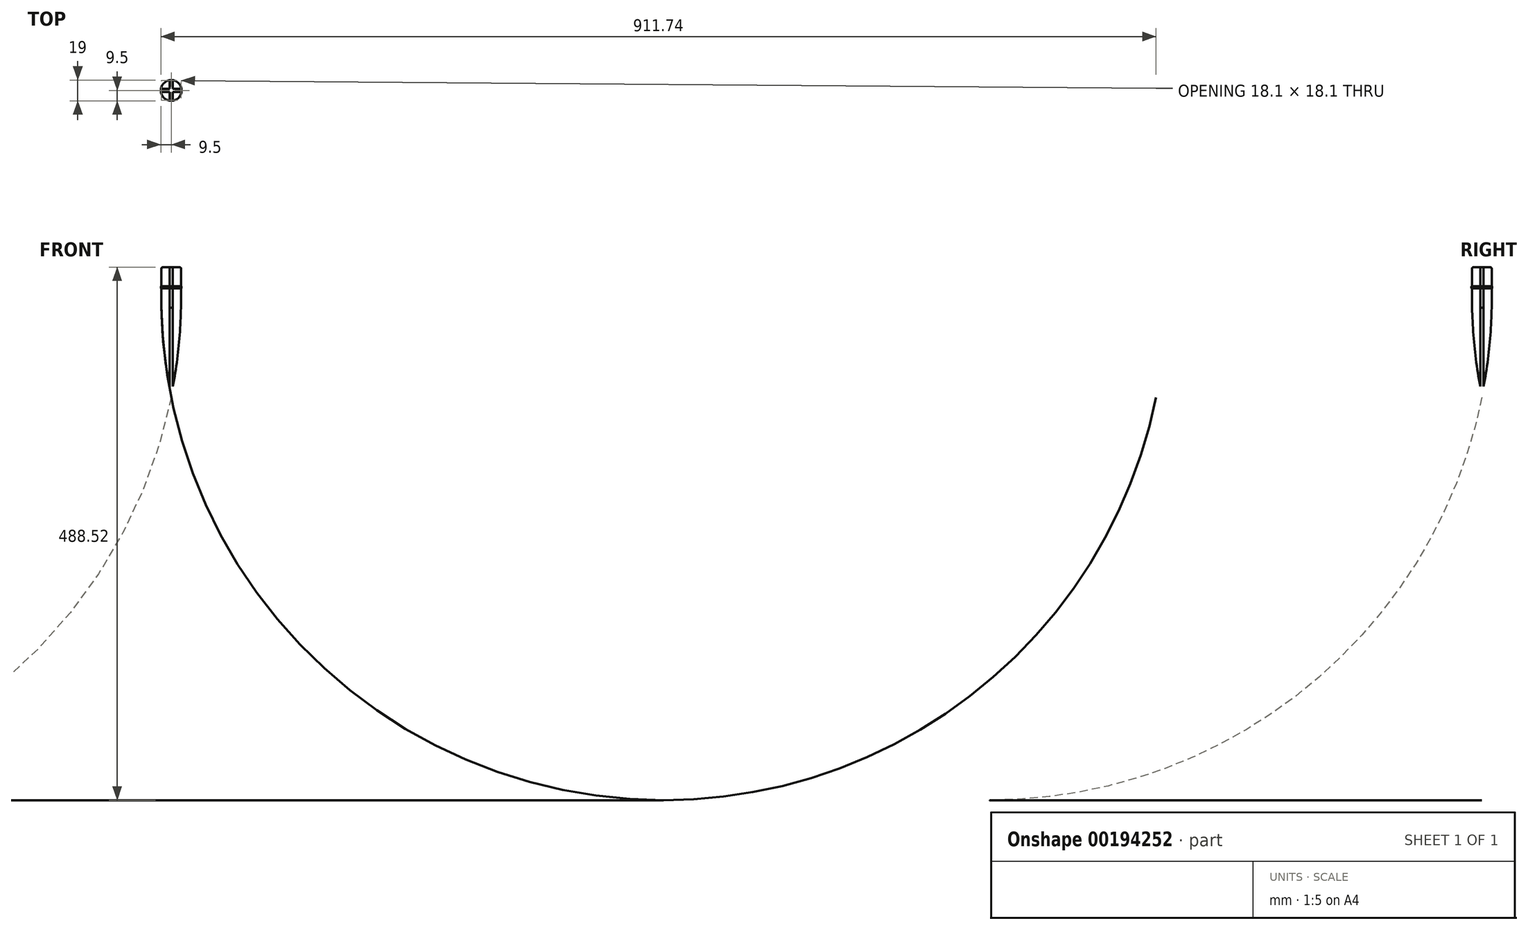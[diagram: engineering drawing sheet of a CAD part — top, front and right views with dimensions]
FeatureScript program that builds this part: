
annotation { "Feature Type Name" : "Feature", "Feature Type Description" : "" }
export const myFeature = defineFeature(function(context is Context, id is Id, definition is map)
    precondition{}
    {
        {
            var Q0;
            Q0=qCreatedBy(makeId("Top.planeOp"),FACE);
            var sketch = newSketch(context, id + "F0", { "sketchPlane" : qUnion([Q0])});
            skCircle(sketch, "E0", {"center": v(0, 0) * mm, "radius": 9.05 * mm});
            skSolve(sketch);
        }
        {
            var Q0;
            Q0 = qSketchRegion(id + "F0", true);
            extrude(context, id + "F1", {"entities" : qUnion([Q0]), "depth" : 17.5 * mm});
        }
        {
            var Q0;
            Q0=makeQuery(id+"F1.opExtrude","CAP_EDGE",EDGE,{"disambiguationData":[OSD([sQuery(id+"F0.wireOp",EDGE,"E0")])],"isStart":false});
            fillet(context, id + "F2", {"entities" : qUnion([Q0]), "radius" : 1.5 * mm, "tangentPropagation" : true, "allowEdgeOverflow" : false});
        }
        {
            var Q0;
            Q0=makeQuery(id+"F1.opExtrude","CAP_FACE",FACE,{"disambiguationData":[OSD([sQuery(id+"F0.wireOp",EDGE,"E0")])],"isStart":true});
            var sketch = newSketch(context, id + "F3", { "sketchPlane" : qUnion([Q0])});
            skLineSegment(sketch, "E1", {"start": v(9.05, 1.4) * mm, "end": v(0, 1.4) * mm});
            skLineSegment(sketch, "E2", {"start": v(9.05, 1.4) * mm, "end": v(9.05, 0) * mm});
            skLineSegment(sketch, "E3.MirrorCS", {"start": v(1.4, 9.05) * mm, "end": v(1.4, 0) * mm});
            skLineSegment(sketch, "E4.MirrorCS", {"start": v(1.4, 9.05) * mm, "end": v(0, 9.05) * mm});
            skLineSegment(sketch, "E5.MirrorCS", {"start": v(-9.05, 1.4) * mm, "end": v(0, 1.4) * mm});
            skLineSegment(sketch, "E6.MirrorCS", {"start": v(-1.4, 9.05) * mm, "end": v(-1.4, 0) * mm});
            skLineSegment(sketch, "E7.MirrorCS", {"start": v(-1.4, 9.05) * mm, "end": v(0, 9.05) * mm});
            skLineSegment(sketch, "E8.MirrorCS", {"start": v(-9.05, 1.4) * mm, "end": v(-9.05, 0) * mm});
            skLineSegment(sketch, "E9.MirrorCS", {"start": v(9.05, -1.4) * mm, "end": v(0, -1.4) * mm});
            skLineSegment(sketch, "E10.MirrorCS", {"start": v(-9.05, -1.4) * mm, "end": v(0, -1.4) * mm});
            skLineSegment(sketch, "E11.MirrorCS", {"start": v(1.4, -9.05) * mm, "end": v(1.4, 0) * mm});
            skLineSegment(sketch, "E12.MirrorCS", {"start": v(-1.4, -9.05) * mm, "end": v(-1.4, 0) * mm});
            skLineSegment(sketch, "E13.MirrorCS", {"start": v(1.4, -9.05) * mm, "end": v(0, -9.05) * mm});
            skLineSegment(sketch, "E14.MirrorCS", {"start": v(-1.4, -9.05) * mm, "end": v(0, -9.05) * mm});
            skLineSegment(sketch, "E15.MirrorCS", {"start": v(9.05, -1.4) * mm, "end": v(9.05, 0) * mm});
            skLineSegment(sketch, "E16.MirrorCS", {"start": v(-9.05, -1.4) * mm, "end": v(-9.05, 0) * mm});
            skArc(sketch, "E17", {"start": v(9.05, 1.4) * mm, "mid": v(7.85, 7.85) * mm, "end": v(1.4, 9.05) * mm});
            skArc(sketch, "E18", {"start": v(1.4, -9.05) * mm, "mid": v(8.37, -8.37) * mm, "end": v(9.05, -1.4) * mm});
            skArc(sketch, "E19", {"start": v(-9.05, -1.4) * mm, "mid": v(-7.92, -7.92) * mm, "end": v(-1.4, -9.05) * mm});
            skArc(sketch, "E20", {"start": v(-1.4, 9.05) * mm, "mid": v(-11.13, 11.13) * mm, "end": v(-9.05, 1.4) * mm});
            skSolve(sketch);
        }
        {
            var Q0;
            {var subQ0=sQuery(id+"F3.wireOp",EDGE,"E2");Q0=makeQuery(id+"F3.imprint","IMPRINT",FACE,{"disambiguationData":[TD([[makeQuery(id+"F3.imprint","IMPRINT",EDGE,{"derivedFrom":subQ0}),-1.0]])]});}
            var Q1;
            {var subQ0=sQuery(id+"F3.wireOp",EDGE,"E4.MirrorCS");Q1=makeQuery(id+"F3.imprint","IMPRINT",FACE,{"disambiguationData":[TD([[makeQuery(id+"F3.imprint","IMPRINT",EDGE,{"derivedFrom":subQ0}),1.0]])]});}
            var Q2;
            {var subQ0=sQuery(id+"F3.wireOp",EDGE,"E8.MirrorCS");Q2=makeQuery(id+"F3.imprint","IMPRINT",FACE,{"disambiguationData":[TD([[makeQuery(id+"F3.imprint","IMPRINT",EDGE,{"derivedFrom":subQ0}),1.0]])]});}
            var Q3;
            {var subQ0=sQuery(id+"F3.wireOp",EDGE,"E7.MirrorCS");Q3=makeQuery(id+"F3.imprint","IMPRINT",FACE,{"disambiguationData":[TD([[makeQuery(id+"F3.imprint","IMPRINT",EDGE,{"derivedFrom":subQ0}),-1.0]])]});}
            var Q4;
            {var subQ0=sQuery(id+"F3.wireOp",EDGE,"E15.MirrorCS");Q4=makeQuery(id+"F3.imprint","IMPRINT",FACE,{"disambiguationData":[TD([[makeQuery(id+"F3.imprint","IMPRINT",EDGE,{"derivedFrom":subQ0}),1.0]])]});}
            var Q5;
            {var subQ0=sQuery(id+"F3.wireOp",EDGE,"E16.MirrorCS");Q5=makeQuery(id+"F3.imprint","IMPRINT",FACE,{"disambiguationData":[TD([[makeQuery(id+"F3.imprint","IMPRINT",EDGE,{"derivedFrom":subQ0}),-1.0]])]});}
            var Q6;
            {var subQ0=sQuery(id+"F3.wireOp",EDGE,"E13.MirrorCS");Q6=makeQuery(id+"F3.imprint","IMPRINT",FACE,{"disambiguationData":[TD([[makeQuery(id+"F3.imprint","IMPRINT",EDGE,{"derivedFrom":subQ0}),-1.0]])]});}
            var Q7;
            {var subQ0=sQuery(id+"F3.wireOp",EDGE,"E14.MirrorCS");Q7=makeQuery(id+"F3.imprint","IMPRINT",FACE,{"disambiguationData":[TD([[makeQuery(id+"F3.imprint","IMPRINT",EDGE,{"derivedFrom":subQ0}),1.0]])]});}
            var Q8;
            {var subQ0=sQuery(id+"F3.wireOp",EDGE,"E3.MirrorCS");var subQ1=sQuery(id+"F3.wireOp",EDGE,"E1");var subQ2=makeQuery(id+"F3.imprint","INTERSECT",VERTEX,{"derivedFrom":[subQ1,subQ0]});Q8=makeQuery(id+"F3.imprint","IMPRINT",FACE,{"disambiguationData":[TD([[makeQuery(id+"F3.imprint","IMPRINT",EDGE,{"disambiguationData":[TD([[subQ2,1.0]])],"derivedFrom":subQ1}),-1.0]])]});}
            var Q9;
            {var subQ0=sQuery(id+"F3.wireOp",EDGE,"E11.MirrorCS");var subQ1=sQuery(id+"F3.wireOp",EDGE,"E9.MirrorCS");var subQ2=makeQuery(id+"F3.imprint","INTERSECT",VERTEX,{"derivedFrom":[subQ1,subQ0]});Q9=makeQuery(id+"F3.imprint","IMPRINT",FACE,{"disambiguationData":[TD([[makeQuery(id+"F3.imprint","IMPRINT",EDGE,{"disambiguationData":[TD([[subQ2,1.0]])],"derivedFrom":subQ1}),1.0]])]});}
            var Q10;
            {var subQ0=sQuery(id+"F3.wireOp",EDGE,"E12.MirrorCS");var subQ1=sQuery(id+"F3.wireOp",EDGE,"E10.MirrorCS");var subQ2=makeQuery(id+"F3.imprint","INTERSECT",VERTEX,{"derivedFrom":[subQ1,subQ0]});Q10=makeQuery(id+"F3.imprint","IMPRINT",FACE,{"disambiguationData":[TD([[makeQuery(id+"F3.imprint","IMPRINT",EDGE,{"disambiguationData":[TD([[subQ2,1.0]])],"derivedFrom":subQ1}),-1.0]])]});}
            var Q11;
            {var subQ0=sQuery(id+"F3.wireOp",EDGE,"E6.MirrorCS");var subQ1=sQuery(id+"F3.wireOp",EDGE,"E5.MirrorCS");var subQ2=makeQuery(id+"F3.imprint","INTERSECT",VERTEX,{"derivedFrom":[subQ1,subQ0]});Q11=makeQuery(id+"F3.imprint","IMPRINT",FACE,{"disambiguationData":[TD([[makeQuery(id+"F3.imprint","IMPRINT",EDGE,{"disambiguationData":[TD([[subQ2,1.0]])],"derivedFrom":subQ1}),1.0]])]});}
            extrude(context, id + "F4", {"entities" : qUnion([Q0, Q1, Q2, Q3, Q4, Q5, Q6, Q7, Q8, Q9, Q10, Q11]), "operationType" : NewBodyOperationType.REMOVE, "oppositeDirection" : true, "depth" : 25 * mm});
        }
        {
            var Q0;
            Q0=makeQuery(id+"F1.opExtrude","CAP_FACE",FACE,{"disambiguationData":[OSD([sQuery(id+"F0.wireOp",EDGE,"E0")])],"isStart":true});
            var sketch = newSketch(context, id + "F5", { "sketchPlane" : qUnion([Q0])});
            skCircle(sketch, "E21", {"center": v(0, 0) * mm, "radius": 9.5 * mm});
            skSolve(sketch);
        }
        {
            var Q0;
            Q0 = qSketchRegion(id + "F5", true);
            extrude(context, id + "F6", {"entities" : qUnion([Q0]), "operationType" : NewBodyOperationType.ADD, "depth" : 2 * mm});
        }
        {
            var Q0;
            Q0=makeQuery(id+"F6.opExtrude","CAP_FACE",FACE,{"disambiguationData":[OSD([sQuery(id+"F5.wireOp",EDGE,"E21")])],"isStart":false});
            var sketch = newSketch(context, id + "F7", { "sketchPlane" : qUnion([Q0])});
            skCircle(sketch, "E22", {"center": v(0, 0) * mm, "radius": 9.05 * mm});
            skSolve(sketch);
        }
        {
            var Q0;
            Q0 = qSketchRegion(id + "F7", true);
            extrude(context, id + "F8", {"entities" : qUnion([Q0]), "operationType" : NewBodyOperationType.ADD, "depth" : 100 * mm});
        }
        {
            var Q0;
            Q0=qCreatedBy(makeId("Front.planeOp"),FACE);
            var sketch = newSketch(context, id + "F9", { "sketchPlane" : qUnion([Q0])});
            skLineSegment(sketch, "E23", {"start": v(0, -2) * mm, "end": v(0, 0) * mm});
            skLineSegment(sketch, "E24", {"start": v(0, -2) * mm, "end": v(0, -102) * mm});
            skArc(sketch, "E25", {"start": v(-9.05, -2) * mm, "mid": v(-7.26, -52.25) * mm, "end": v(0, -102) * mm});
            skLineSegment(sketch, "E26", {"start": v(0, -102) * mm, "end": v(-9.05, -102) * mm});
            skLineSegment(sketch, "E27", {"start": v(-9.05, -102) * mm, "end": v(-9.05, -2) * mm});
            skArc(sketch, "E28.MirrorCS", {"start": v(9.05, -2) * mm, "mid": v(7.26, -52.25) * mm, "end": v(0, -102) * mm});
            skLineSegment(sketch, "E29.MirrorCS", {"start": v(9.05, -102) * mm, "end": v(9.05, -2) * mm});
            skLineSegment(sketch, "E30.MirrorCS", {"start": v(0, -102) * mm, "end": v(9.05, -102) * mm});
            skSolve(sketch);
        }
        {
            var Q0;
            Q0 = qSketchRegion(id + "F9", true);
            var Q1;
            Q1=sQuery(id+"F9.wireOp",EDGE,"E24");
            revolve(context, id + "F10", {"operationType" : NewBodyOperationType.REMOVE, "entities" : qUnion([Q0]), "axis" : qUnion([Q1]), "revolveType" : RevolveType.ONE_DIRECTION, "angle" : 180 * degree});
        }
        {
            var Q0;
            Q0=makeQuery(id+"F6.opExtrude","CAP_FACE",FACE,{"disambiguationData":[OSD([sQuery(id+"F5.wireOp",EDGE,"E21")])],"isStart":false});
            var sketch = newSketch(context, id + "F11", { "sketchPlane" : qUnion([Q0])});
            skLineSegment(sketch, "E31.0.0", {"start": v(-1.4, -7.42) * mm, "end": v(-1.4, -1.4) * mm});
            skLineSegment(sketch, "E31.0.1", {"start": v(-1.4, -1.4) * mm, "end": v(-7.42, -1.4) * mm});
            skLineSegment(sketch, "E31.0.3", {"start": v(-7.42, 1.4) * mm, "end": v(-1.4, 1.4) * mm});
            skLineSegment(sketch, "E31.0.4", {"start": v(-1.4, 1.4) * mm, "end": v(-1.4, 7.42) * mm});
            skLineSegment(sketch, "E31.0.6", {"start": v(1.4, 7.42) * mm, "end": v(1.4, 1.4) * mm});
            skLineSegment(sketch, "E31.0.7", {"start": v(1.4, 1.4) * mm, "end": v(7.42, 1.4) * mm});
            skLineSegment(sketch, "E31.0.9", {"start": v(7.42, -1.4) * mm, "end": v(1.4, -1.4) * mm});
            skLineSegment(sketch, "E31.0.10", {"start": v(1.4, -1.4) * mm, "end": v(1.4, -7.42) * mm});
            skLineSegment(sketch, "E32", {"start": v(7.42, 1.4) * mm, "end": v(12.42, 1.4) * mm});
            skLineSegment(sketch, "E33", {"start": v(7.42, -1.4) * mm, "end": v(12.42, -1.4) * mm});
            skLineSegment(sketch, "E34.MirrorCS", {"start": v(1.4, 7.42) * mm, "end": v(1.4, 12.42) * mm});
            skLineSegment(sketch, "E35.MirrorCS", {"start": v(-1.4, 7.42) * mm, "end": v(-1.4, 12.42) * mm});
            skLineSegment(sketch, "E36.MirrorCS", {"start": v(-7.42, 1.4) * mm, "end": v(-12.42, 1.4) * mm});
            skLineSegment(sketch, "E37.MirrorCS", {"start": v(-7.42, -1.4) * mm, "end": v(-12.42, -1.4) * mm});
            skLineSegment(sketch, "E38.MirrorCS", {"start": v(1.4, -7.42) * mm, "end": v(1.4, -12.42) * mm});
            skLineSegment(sketch, "E39.MirrorCS", {"start": v(-1.4, -7.42) * mm, "end": v(-1.4, -12.42) * mm});
            skLineSegment(sketch, "E40", {"start": v(1.4, -12.42) * mm, "end": v(12.42, -1.4) * mm});
            skLineSegment(sketch, "E41", {"start": v(-1.4, -12.42) * mm, "end": v(-12.42, -1.4) * mm});
            skLineSegment(sketch, "E42", {"start": v(12.42, 1.4) * mm, "end": v(1.4, 12.42) * mm});
            skLineSegment(sketch, "E43", {"start": v(-1.4, 12.42) * mm, "end": v(-12.42, 1.4) * mm});
            skSolve(sketch);
        }
        {
            var Q0;
            Q0 = qSketchRegion(id + "F11", true);
            extrude(context, id + "F12", {"entities" : qUnion([Q0]), "operationType" : NewBodyOperationType.REMOVE, "endBound" : BoundingType.THROUGH_ALL, "depth" : 25 * mm});
        }
    });
